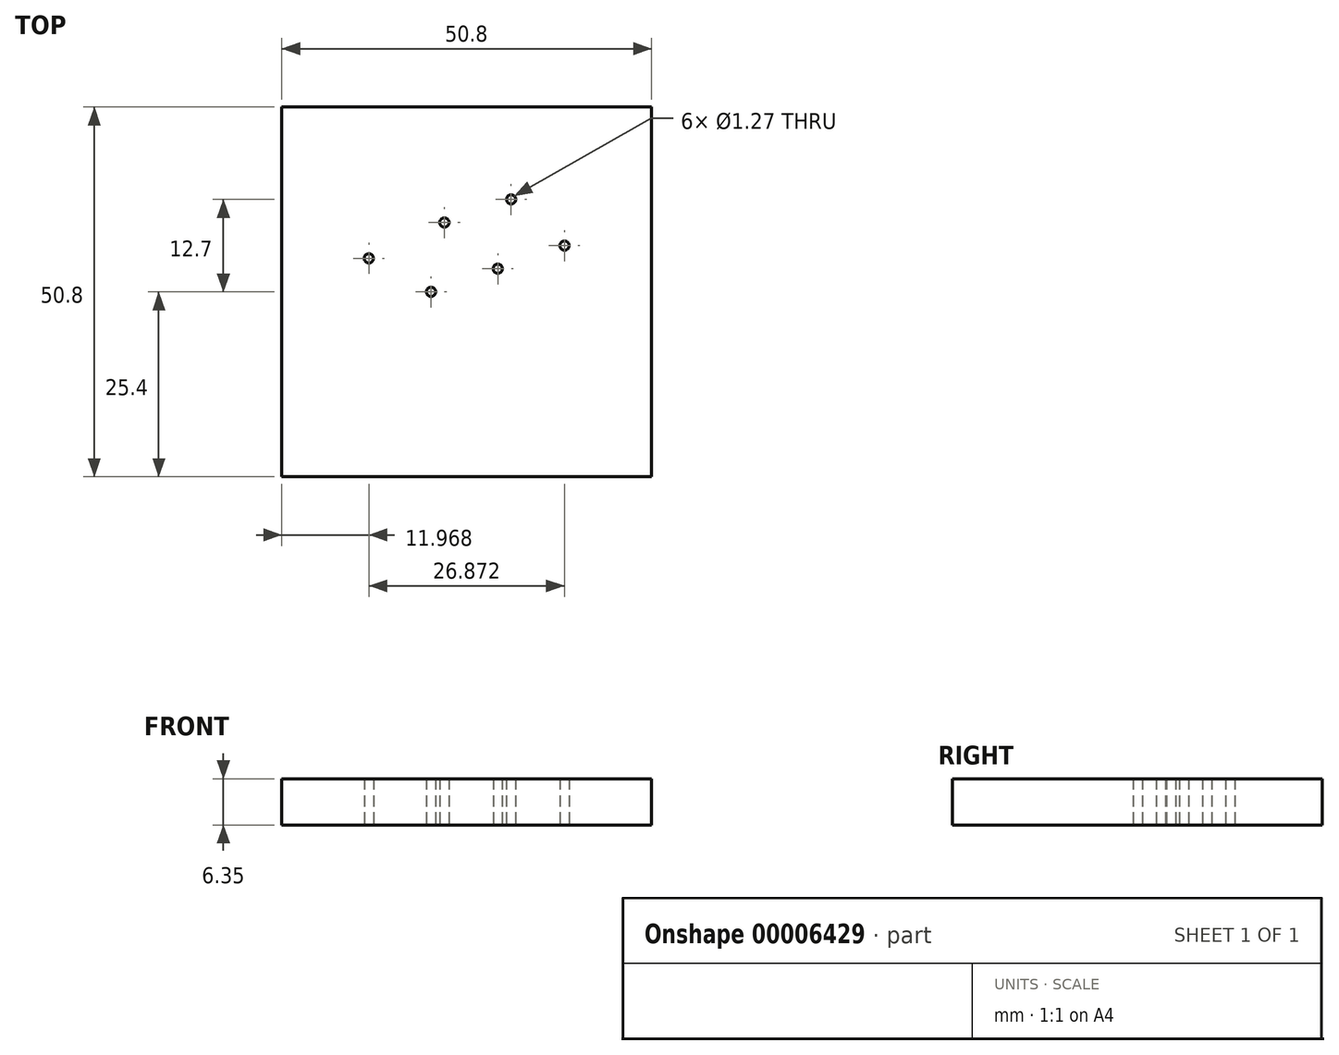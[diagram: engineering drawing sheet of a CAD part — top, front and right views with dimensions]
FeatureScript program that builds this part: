
annotation { "Feature Type Name" : "Feature", "Feature Type Description" : "" }
export const myFeature = defineFeature(function(context is Context, id is Id, definition is map)
    precondition{}
    {
        {
            var Q0;
            Q0=qCreatedBy(makeId("Top.planeOp"),FACE);
            var sketch = newSketch(context, id + "F0", { "sketchPlane" : qUnion([Q0])});
            skCircle(sketch, "E0", {"center": v(-6.86, 6.35) * mm, "radius": 0.64 * mm});
            skCircle(sketch, "E1", {"center": v(-25.2, 0) * mm, "radius": 0.64 * mm});
            skCircle(sketch, "E2", {"center": v(-23.36, 9.53) * mm, "radius": 0.64 * mm});
            skCircle(sketch, "E3", {"center": v(-16.03, 3.17) * mm, "radius": 0.64 * mm});
            skCircle(sketch, "E4", {"center": v(-33.73, 4.6) * mm, "radius": 0.64 * mm});
            skLineSegment(sketch, "E5.bottom", {"start": v(-45.7, 25.4) * mm, "end": v(5.1, 25.4) * mm});
            skLineSegment(sketch, "E5.top", {"start": v(-45.7, -25.4) * mm, "end": v(5.1, -25.4) * mm});
            skLineSegment(sketch, "E5.left", {"start": v(-45.7, 25.4) * mm, "end": v(-45.7, -25.4) * mm});
            skLineSegment(sketch, "E5.right", {"start": v(5.1, 25.4) * mm, "end": v(5.1, -25.4) * mm});
            skCircle(sketch, "E6", {"center": v(-14.2, 12.7) * mm, "radius": 0.64 * mm});
            skLineSegment(sketch, "E7", {"start": v(-25.07, 0.62) * mm, "end": v(-23.48, 8.9) * mm, "construction": true});
            skLineSegment(sketch, "E8", {"start": v(-24.6, 0.2) * mm, "end": v(-16.63, 2.97) * mm, "construction": true});
            skLineSegment(sketch, "E9", {"start": v(-22.88, 9.1) * mm, "end": v(-16.5, 3.6) * mm, "construction": true});
            skLineSegment(sketch, "E10", {"start": v(-22.76, 9.73) * mm, "end": v(-14.8, 12.5) * mm, "construction": true});
            skLineSegment(sketch, "E11", {"start": v(-14.31, 12.08) * mm, "end": v(-15.9, 3.8) * mm, "construction": true});
            skLineSegment(sketch, "E12", {"start": v(-15.43, 3.38) * mm, "end": v(-7.46, 6.14) * mm, "construction": true});
            skLineSegment(sketch, "E13", {"start": v(-13.71, 12.28) * mm, "end": v(-7.34, 6.77) * mm, "construction": true});
            skLineSegment(sketch, "E14", {"start": v(-25.75, 0.3) * mm, "end": v(-33.17, 4.3) * mm, "construction": true});
            skLineSegment(sketch, "E15", {"start": v(-34.37, 4.6) * mm, "end": v(-45.7, 4.6) * mm, "construction": true});
            skLineSegment(sketch, "E16", {"start": v(-6.22, 6.35) * mm, "end": v(5.1, 6.35) * mm, "construction": true});
            skSolve(sketch);
        }
        {
            var Q0;
            Q0=qSketchRegion(id+"F0",true);
            extrude(context, id + "F1", {"entities" : qUnion([Q0]), "depth" : 6.35 * mm});
        }
    });
